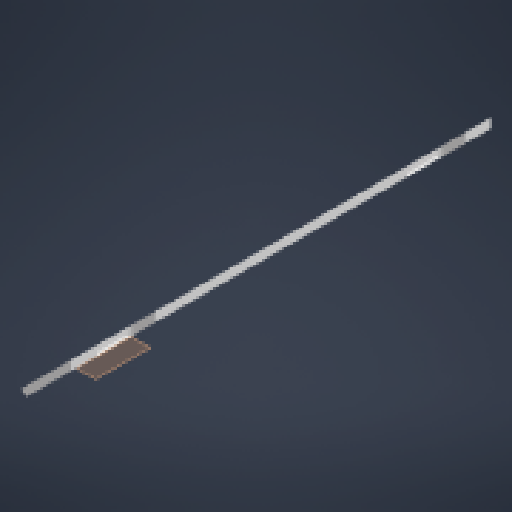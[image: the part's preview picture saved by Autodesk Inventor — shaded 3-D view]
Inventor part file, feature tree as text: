
AUTODESK INVENTOR PART (.ipt)
format: ipt  version: 2023 (Build 270158000, 158)  size: 175,104 bytes
history: native  units: in
note: dims shown in document units (in); Inventor stores cm internally (conversion verified against a paired STEP export)
features: reference x10, other x7, sketch x3, plane x2, extrude x2, hole x1, projected_geometry x1
ambient origin geometry x8: Origin, YZ Plane, XZ Plane, XY Plane, X Axis, Y Axis, Z Axis, Center Point
bodies: Solid1 (feature_tree)
feature tree (26):
  sketch  "Sketch1"  dims[d0=1.1811in d1=0.1181in]
  plane  "Work Plane1"
  extrude  "Extrusion1"  Depth=0.1181in
  plane  "Work Plane2"
  extrude  "Extrusion2"  Depth=0.0787in
  hole  "Hole1"  [1 undecoded]
  reference  "Reference1"
  reference  "Reference2"
  reference  "Reference3"
  sketch  "Sketch2"  dims[d2=0.3937in d3=0.0in d4=0.0787in]
  reference  "Reference4"
  reference  "Reference5"
  reference  "Reference6"
  projected_geometry  "Projected Loop1"
  sketch  "Sketch3"  dims[d5=0.0787in d6=0.0787in d7=0.0787in d8=0.0787in d9=0.0in d10=0.0in d11=0.1339in d12=0.2362in d13=0.248in d14=0.0787in d15=90.0deg d16=0.315in d17=0.8108in]
  reference  "Reference7"
  reference  "Reference8"
  reference  "Reference9"
  reference  "Reference10"
  parser-record x1  (decoder bookkeeping rows leaked as tree rows — omitted from the tree; the rows remain in map.json)
  other  "Placek.iam"
  other  "BokPrawy_MIR:1"
  other  "PLUG:1"
  other  "sds02a-with-sensor:1"
  other  "mocowanie-czujnika-p:1"
  other  "mocowanie-czujniklewy:1"
note: 1 required parameter value undecoded (feature->parameter linkage not recoverable at this tier; creation-order binding heuristic only, values carry confidence <= 0.55)
note: 1 file-system path scrubbed to <path> (originals preserved in map.json)
